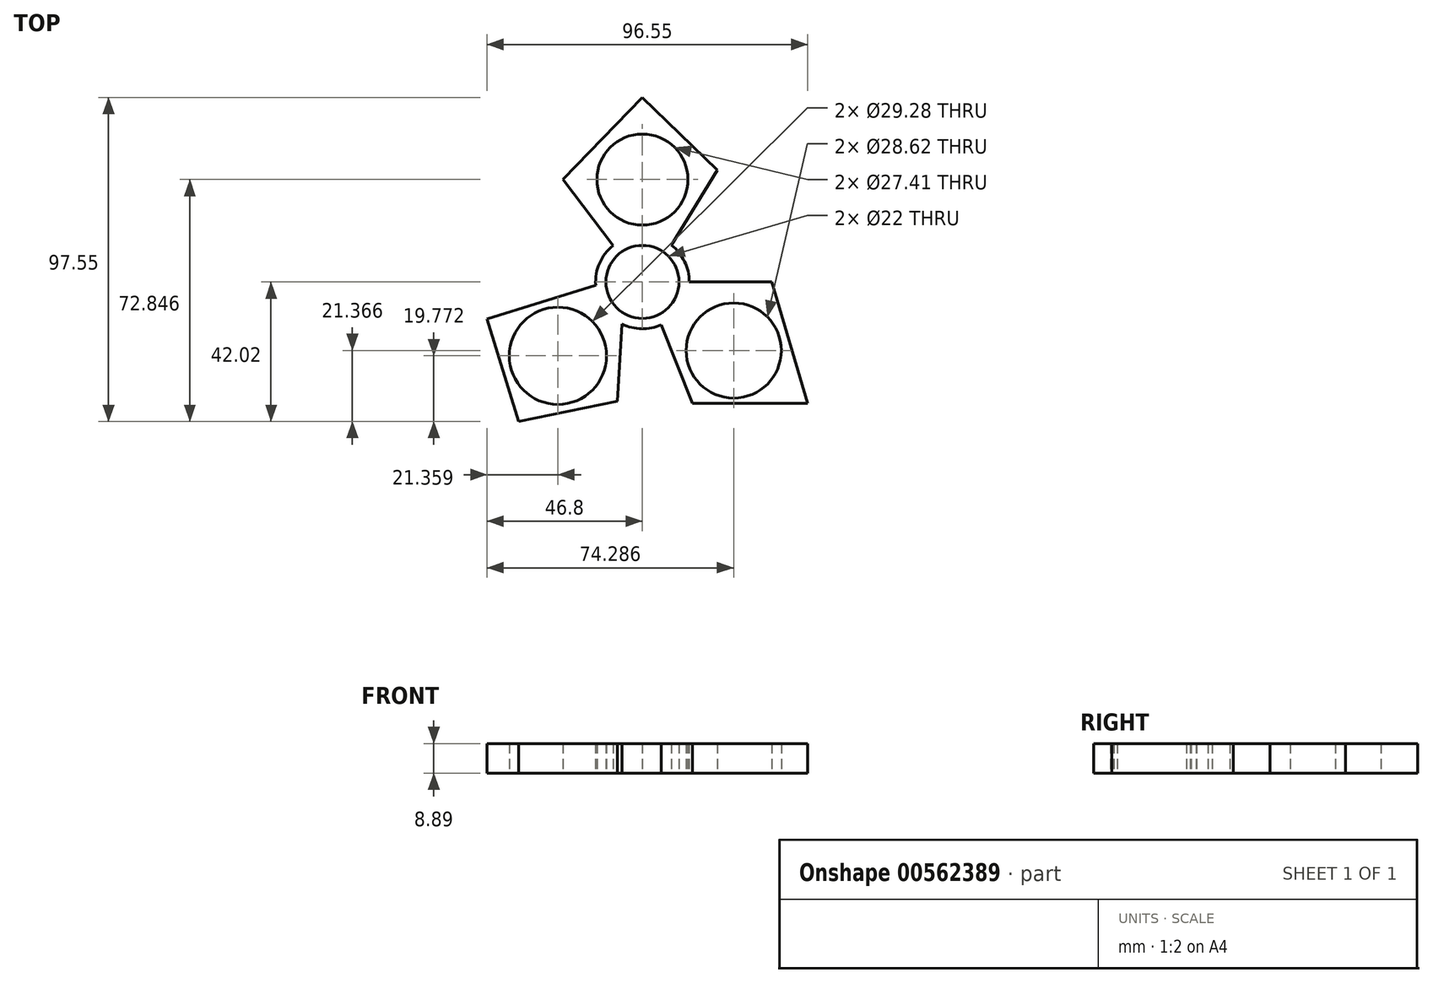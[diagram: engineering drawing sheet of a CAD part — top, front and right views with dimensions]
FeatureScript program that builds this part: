
annotation { "Feature Type Name" : "Feature", "Feature Type Description" : "" }
export const myFeature = defineFeature(function(context is Context, id is Id, definition is map)
    precondition{}
    {
        {
            var Q0;
            Q0=qCreatedBy(makeId("Top.planeOp"),FACE);
            var sketch = newSketch(context, id + "F0", { "sketchPlane" : qUnion([Q0])});
            skCircle(sketch, "E0", {"center": v(0, 0) * mm, "radius": 11 * mm});
            skCircle(sketch, "E1", {"center": v(0, 30.83) * mm, "radius": 11 * mm});
            skCircle(sketch, "E2", {"center": v(0, 30.83) * mm, "radius": 13.7 * mm});
            skLineSegment(sketch, "E3", {"start": v(0, 55.53) * mm, "end": v(-23.88, 30.83) * mm});
            skLineSegment(sketch, "E4", {"start": v(-23.88, 30.83) * mm, "end": v(-6.95, 8.52) * mm});
            skLineSegment(sketch, "E5", {"start": v(0, 55.53) * mm, "end": v(22.53, 33.75) * mm});
            skLineSegment(sketch, "E6", {"start": v(22.53, 33.75) * mm, "end": v(7.12, 8.39) * mm});
            skCircle(sketch, "E7", {"center": v(27.49, -20.65) * mm, "radius": 11 * mm});
            skCircle(sketch, "E8", {"center": v(27.49, -20.65) * mm, "radius": 14.31 * mm});
            skCircle(sketch, "E9", {"center": v(-25.44, -22.25) * mm, "radius": 11 * mm});
            skCircle(sketch, "E10", {"center": v(-25.44, -22.25) * mm, "radius": 14.64 * mm});
            skLineSegment(sketch, "E11", {"start": v(-37.24, -42.02) * mm, "end": v(-7.59, -35.96) * mm});
            skLineSegment(sketch, "E12", {"start": v(-37.24, -42.02) * mm, "end": v(-46.8, -11.09) * mm});
            skLineSegment(sketch, "E13", {"start": v(-46.8, -11.09) * mm, "end": v(-11, 0) * mm});
            skLineSegment(sketch, "E14", {"start": v(-7.59, -35.96) * mm, "end": v(-5.87, -9.3) * mm});
            skLineSegment(sketch, "E15", {"start": v(49.75, -36.6) * mm, "end": v(15.05, -36.6) * mm});
            skLineSegment(sketch, "E16", {"start": v(15.05, -36.6) * mm, "end": v(4.5, -10.03) * mm});
            skLineSegment(sketch, "E17", {"start": v(49.75, -36.6) * mm, "end": v(38.94, 0) * mm});
            skLineSegment(sketch, "E18", {"start": v(38.94, 0) * mm, "end": v(11, 0) * mm});
            skCircle(sketch, "E19", {"center": v(0, 0) * mm, "radius": 14.1 * mm});
            skSolve(sketch);
        }
        {
            var Q0;
            Q0 = qSketchRegion(id + "F0", true);
            extrude(context, id + "F1", {"entities" : qUnion([Q0]), "depth" : 8.9 * mm, "offsetDistance" : 25.4 * mm});
        }
    });
